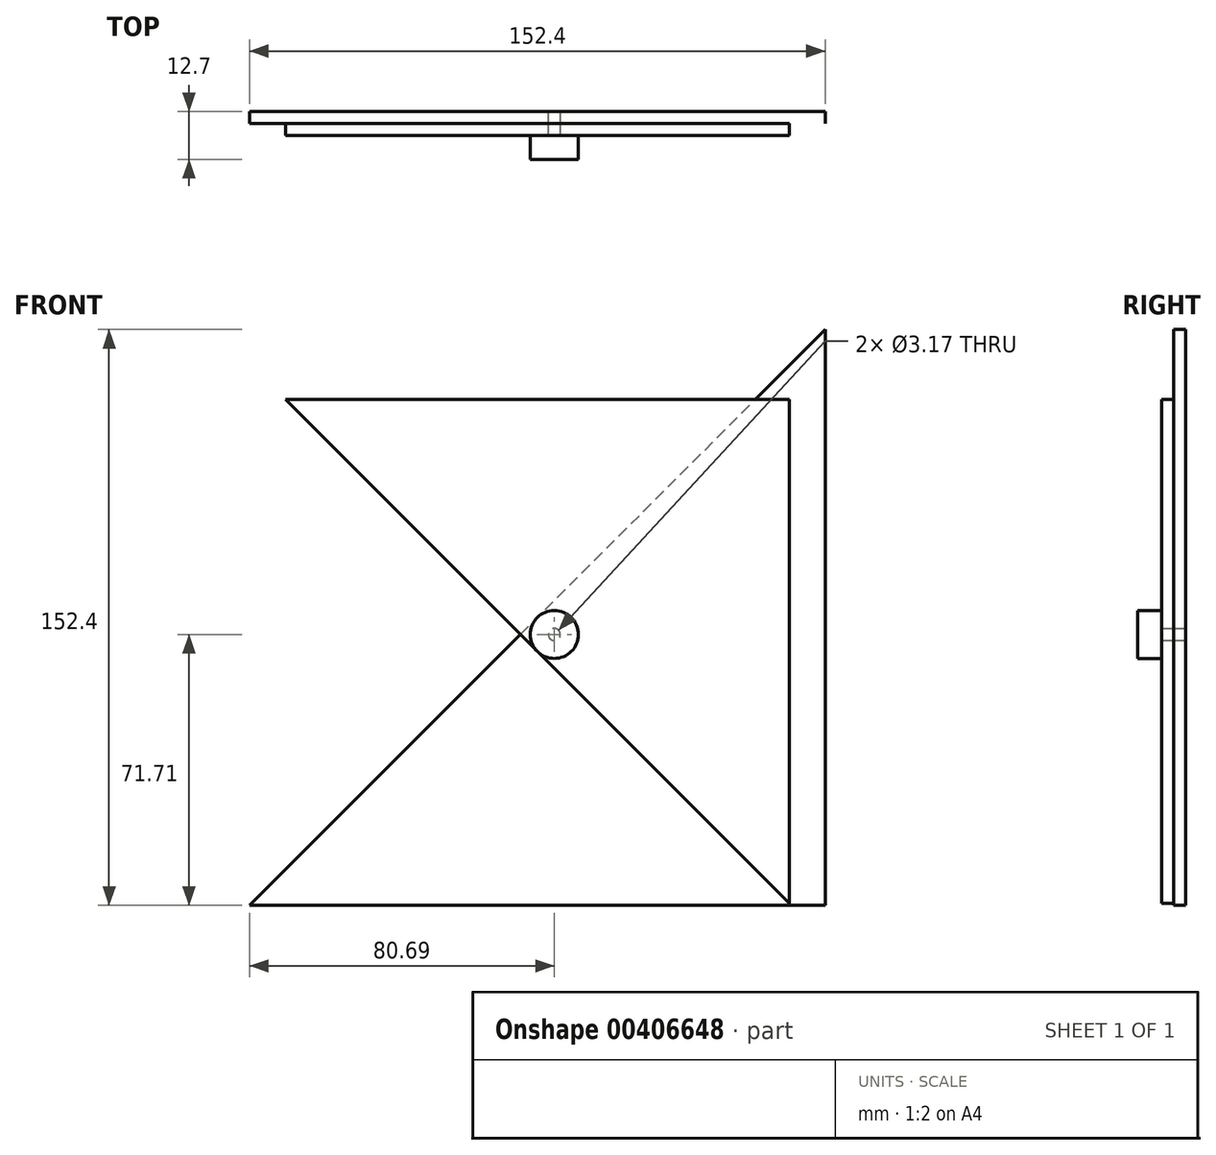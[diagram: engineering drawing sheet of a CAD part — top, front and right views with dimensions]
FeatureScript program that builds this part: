
annotation { "Feature Type Name" : "Feature", "Feature Type Description" : "" }
export const myFeature = defineFeature(function(context is Context, id is Id, definition is map)
    precondition{}
    {
        {
            var Q0;
            Q0=qCreatedBy(makeId("Front.planeOp"),FACE);
            var sketch = newSketch(context, id + "F0", { "sketchPlane" : qUnion([Q0])});
            skLineSegment(sketch, "E0.bottom", {"start": v(-76.2, 76.2) * mm, "end": v(76.2, 76.2) * mm, "construction": true});
            skLineSegment(sketch, "E0.top", {"start": v(-76.2, -76.2) * mm, "end": v(76.2, -76.2) * mm});
            skLineSegment(sketch, "E0.left", {"start": v(-76.2, 76.2) * mm, "end": v(-76.2, -76.2) * mm, "construction": true});
            skLineSegment(sketch, "E0.right", {"start": v(76.2, 76.2) * mm, "end": v(76.2, -76.2) * mm});
            skPoint(sketch, "E0.middle", {"position": v(0, 0) * mm});
            skLineSegment(sketch, "E1", {"start": v(-76.2, -76.2) * mm, "end": v(76.2, 76.2) * mm});
            skLineSegment(sketch, "E2", {"start": v(-76.2, 76.2) * mm, "end": v(76.2, -76.2) * mm, "construction": true});
            skCircle(sketch, "E3", {"center": v(4.5, -4.5) * mm, "radius": 6.35 * mm, "construction": true});
            skCircle(sketch, "E4", {"center": v(4.5, -4.5) * mm, "radius": 1.59 * mm});
            skSolve(sketch);
        }
        {
            var Q0;
            Q0=qSketchRegion(id+"F0",true);
            var Q1;
            Q1=sQuery(id+"F0.wireOp",EDGE,"E0.bottom");
            var Q2;
            Q2=sQuery(id+"F0.wireOp",EDGE,"E0.left");
            extrude(context, id + "F1", {"entities" : qUnion([Q0]), "surfaceEntities" : qUnion([Q1, Q2]), "depth" : 3.17 * mm});
        }
        {
            var Q0;
            Q0=sQuery(id+"F0.wireOp",VERTEX,"E4.center");
            var Q1;
            Q1=qCreatedBy(makeId("Top.planeOp"),FACE);
            cPlane(context, id + "F2", {"entities" : qUnion([Q0, Q1]), "cplaneType" : CPlaneType.PLANE_POINT, "offset" : 25.4 * mm, "width" : 152.4 * mm, "height" : 152.4 * mm});
        }
        {
            var Q0;
            Q0=qCreatedBy(id+"F2.planeOp",FACE);
            var sketch = newSketch(context, id + "F3", { "sketchPlane" : qUnion([Q0])});
            skPoint(sketch, "E5.0", {"position": v(4.5, 0) * mm});
            skLineSegment(sketch, "E6", {"start": v(4.5, 0) * mm, "end": v(4.5, -119.12) * mm});
            skSolve(sketch);
        }
        {
            var Q0;
            Q0=makeQuery(id+"F1.opExtrude","SWEPT_BODY",BODY,{"disambiguationData":[OSD([sQuery(id+"F0.wireOp",EDGE,"E0.top"),sQuery(id+"F0.wireOp",EDGE,"E0.right"),sQuery(id+"F0.wireOp",EDGE,"E1"),sQuery(id+"F0.wireOp",EDGE,"E4")])]});
            var Q1;
            Q1=sQuery(id+"F3.wireOp",EDGE,"E6");
            var Q2;
            Q2=sQuery(id+"F3.wireOp",EDGE,"E6");
            transform(context, id + "F4", {"entities" : qUnion([Q0]), "transformType" : TransformType.ROTATION, "transformAxis" : qUnion([Q2]), "angle" : 90 * degree, "makeCopy" : true});
        }
        {
            var Q0;
            Q0=makeQuery(id+"F4.opPattern","COPY",BODY,{"derivedFrom":makeQuery(id+"F1.opExtrude","SWEPT_BODY",BODY,{"disambiguationData":[OSD([sQuery(id+"F0.wireOp",EDGE,"E0.top"),sQuery(id+"F0.wireOp",EDGE,"E0.right"),sQuery(id+"F0.wireOp",EDGE,"E1"),sQuery(id+"F0.wireOp",EDGE,"E4")])]}),"instanceName":"1"});
            var Q1;
            Q1=sQuery(id+"F3.wireOp",EDGE,"E6");
            transform(context, id + "F5", {"entities" : qUnion([Q0]), "transformType" : TransformType.TRANSLATION_DISTANCE, "transformDirection" : qUnion([Q1]), "distance" : 3.17 * mm, "makeCopy" : false});
        }
        {
            var Q0;
            Q0=makeQuery(id+"F4.opPattern","COPY",FACE,{"derivedFrom":makeQuery(id+"F1.opExtrude","CAP_FACE",FACE,{"disambiguationData":[OSD([sQuery(id+"F0.wireOp",EDGE,"E0.top"),sQuery(id+"F0.wireOp",EDGE,"E0.right"),sQuery(id+"F0.wireOp",EDGE,"E1"),sQuery(id+"F0.wireOp",EDGE,"E4")])],"isStart":false}),"instanceName":"1"});
            var sketch = newSketch(context, id + "F6", { "sketchPlane" : qUnion([Q0])});
            skCircle(sketch, "E7.1", {"center": v(4.5, -4.5) * mm, "radius": 6.35 * mm});
            skSolve(sketch);
        }
        {
            var Q0;
            Q0=qSketchRegion(id+"F6",true);
            extrude(context, id + "F7", {"entities" : qUnion([Q0]), "depth" : 6.35 * mm});
        }
        {
            var Q0;
            Q0=makeQuery(id+"F4.opPattern","COPY",FACE,{"derivedFrom":makeQuery(id+"F1.opExtrude","CAP_FACE",FACE,{"disambiguationData":[OSD([sQuery(id+"F0.wireOp",EDGE,"E0.top"),sQuery(id+"F0.wireOp",EDGE,"E0.right"),sQuery(id+"F0.wireOp",EDGE,"E1"),sQuery(id+"F0.wireOp",EDGE,"E4")])],"isStart":false}),"instanceName":"1"});
            var sketch = newSketch(context, id + "F8", { "sketchPlane" : qUnion([Q0])});
            skLineSegment(sketch, "E8.0", {"start": v(66.68, -75.66) * mm, "end": v(66.68, 57.7) * mm});
            skLineSegment(sketch, "E8.1", {"start": v(-66.67, 57.7) * mm, "end": v(66.68, 57.7) * mm});
            skLineSegment(sketch, "E9.0", {"start": v(76.2, -85.18) * mm, "end": v(66.68, -75.66) * mm});
            skLineSegment(sketch, "E10.trimOffspring", {"start": v(-66.67, 57.7) * mm, "end": v(-76.2, 67.22) * mm});
            skLineSegment(sketch, "E11.0", {"start": v(-76.2, 67.22) * mm, "end": v(76.2, 67.22) * mm});
            skLineSegment(sketch, "E11.1", {"start": v(76.2, -85.18) * mm, "end": v(76.2, 67.22) * mm});
            skSolve(sketch);
        }
        {
            var Q0;
            Q0 = qSketchRegion(id + "F8", true);
            extrude(context, id + "F9", {"entities" : qUnion([Q0]), "operationType" : NewBodyOperationType.REMOVE, "oppositeDirection" : true, "depth" : 3.17 * mm});
        }
    });
